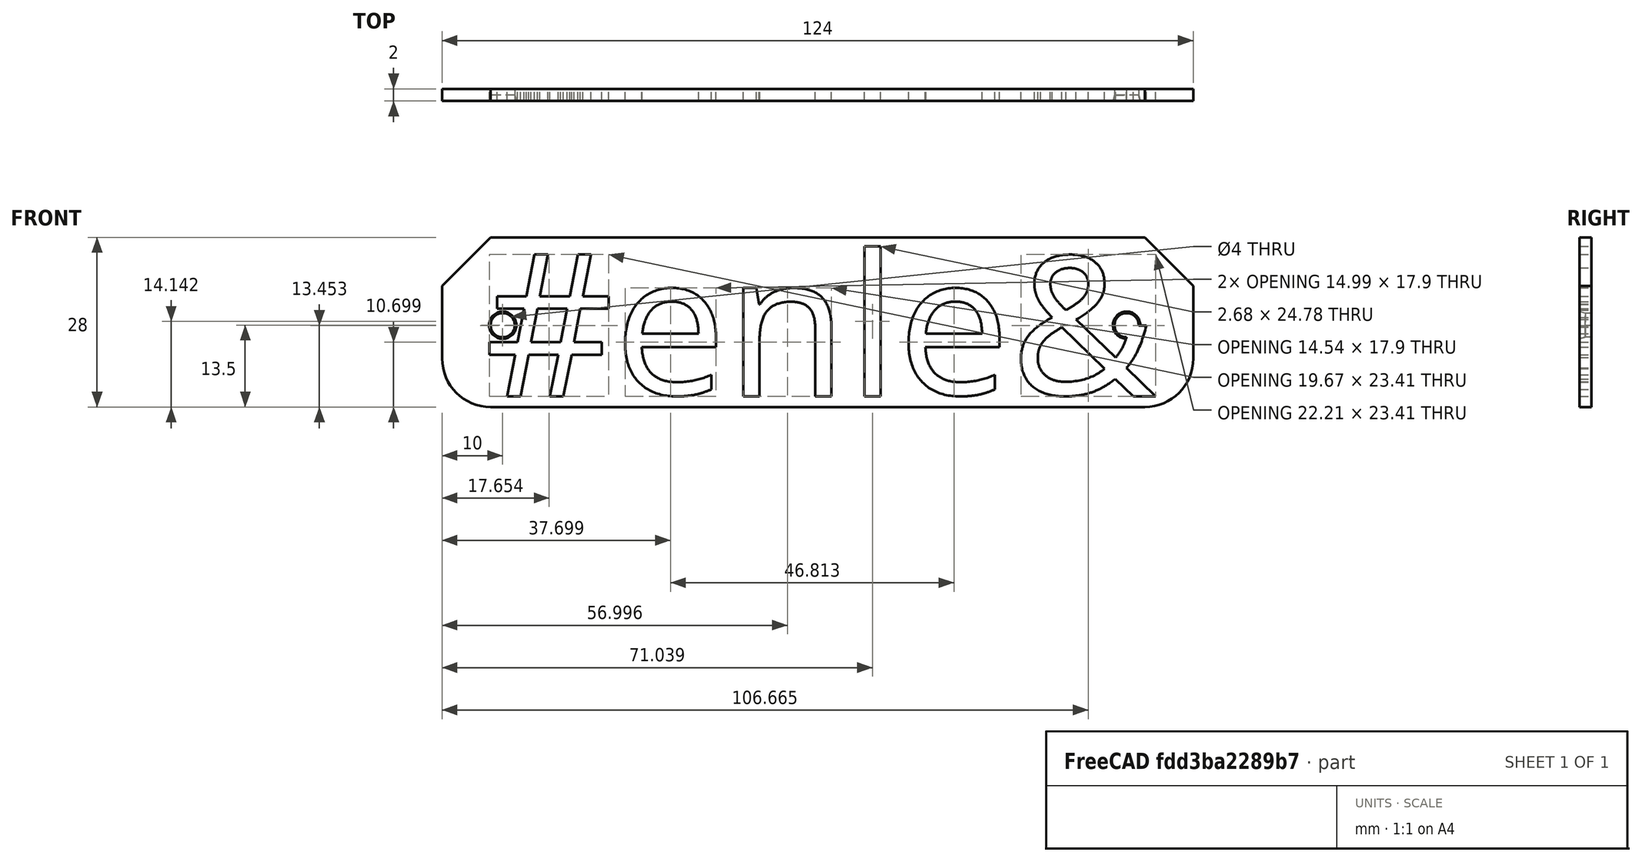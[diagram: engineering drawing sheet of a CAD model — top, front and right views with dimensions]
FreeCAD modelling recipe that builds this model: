
FCSTD DOCUMENT  (FreeCAD 0.19R24276 (Git))
Label: yamahaSR250FuelTankLogo
License: All rights reserved
LicenseURL: http://en.wikipedia.org/wiki/All_rights_reserved
objects: TechDraw::DrawViewDimension×6, Part::Cut×3, TechDraw::DrawProjGroupItem×3, Part::Cylinder×2, Part::Cone×2, Part::MultiFuse×2, TechDraw::DrawSVGTemplate×2, TechDraw::DrawViewPart×2, TechDraw::DrawPage×2, Part::Box×1, Part::Part2DObjectPython×1, Part::Extrusion×1, Part::Chamfer×1, Part::Fillet×1, TechDraw::DrawProjGroup×1, TechDraw::DrawViewAnnotation×1
note: 14 computed .brp shape members not serialized (recipe doc carries the construction recipe); baked Part::Feature solids carry a one-line shape summary decoded from their .brp

FEATURE [Part::Box] Box  label="Cube"
  AttacherType = Attacher::AttachEngine3D
  Height = 28
  Length = 124
  Placement = pos=(0,0,-6.75) rot=(0,0,1;0rad)
  Width = 2
FEATURE [Part::Part2DObjectPython] ShapeString  # Draft 2D object (typed FeaturePython)
  FontFile = <userpath>/Descargas/OpenSans-Regular.ttf
  Placement = pos=(7,0,-5) rot=(1,0,0;1.5708rad)
  Size = 30
  String = #enle&
  Tracking = 0
FEATURE [Part::Extrusion] Extrude
  Base = -> ShapeString
  Dir = (0,2,0)
  DirMode = 0
  FaceMakerClass = Part::FaceMakerExtrusion
  LengthFwd = 0
  LengthRev = 0
  Solid = false
  Symmetric = false
FEATURE [Part::Chamfer] Chamfer
  Base = -> Box
  Edges = 2 edges r=8: [Edge2,Edge6]
FEATURE [Part::Fillet] Fillet
  Base = -> Chamfer
  Edges = 2 edges r=8: [Edge3,Edge13]
FEATURE [Part::Cut] Cut
  Base = -> Fillet
  Tool = -> Extrude
FEATURE [Part::Cylinder] Cylinder
  Angle = 360
  AttacherType = Attacher::AttachEngine3D
  Height = 10
  Placement = pos=(10,2,6.75) rot=(1,0,0;1.5708rad)
  Radius = 2
FEATURE [Part::Cylinder] Cylinder001
  Angle = 360
  AttacherType = Attacher::AttachEngine3D
  Height = 10
  Placement = pos=(113,2,6.75) rot=(1,0,0;1.5708rad)
  Radius = 2
FEATURE [Part::Cone] Cone
  Angle = 360
  AttacherType = Attacher::AttachEngine3D
  Height = 1
  Placement = pos=(10,1,6.75) rot=(1,0,0;1.5708rad)
  Radius1 = 2
  Radius2 = 2.25
FEATURE [Part::Cone] Cone001
  Angle = 360
  AttacherType = Attacher::AttachEngine3D
  Height = 1
  Placement = pos=(113,1,6.75) rot=(1,0,0;1.5708rad)
  Radius1 = 2
  Radius2 = 2.25
FEATURE [Part::MultiFuse] Fusion
  Shapes = -> [Cylinder,Cone]
FEATURE [Part::MultiFuse] Fusion001
  Shapes = -> [Cylinder001,Cone001]
FEATURE [Part::Cut] Cut001
  Base = -> Cut
  Tool = -> Fusion
FEATURE [Part::Cut] Cut002
  Base = -> Cut001
  Tool = -> Fusion001
FEATURE [TechDraw::DrawSVGTemplate] Template
  EditableTexts = Designed_by_Name=<owner>; Drawing_number=001; FC-Date=-; FC-SC=1:1; FC-SH=1/2; FC-Title=SR250FuelTankLogo; Subtitle=Logo Deposito SR250; Weight=<100gr
  Height = 210
  Orientation = 1
  Width = 297
FEATURE [TechDraw::DrawSVGTemplate] Template001
  EditableTexts = Designed_by_Name=<owner>; Drawing_number=001; FC-Date=-; FC-SC=1:1; FC-SH=2/2; FC-Title=SR250FuelTankLogo; Subtitle=Logo Deposito SR250; Weight=<100gr
  Height = 210
  Orientation = 1
  Width = 297
FEATURE [TechDraw::DrawViewPart] View
  CoarseView = false
  Direction = (0.577,-0.577,0.577)
  Focus = 100
  HardHidden = false
  IsoCount = 0
  IsoHidden = false
  IsoVisible = false
  LockPosition = false
  Perspective = false
  Rotation = 0
  ScaleType = 0
  SeamHidden = false
  SeamVisible = true
  SmoothHidden = false
  SmoothVisible = true
  Source = -> [Cut002]
  X = 222.526
  XDirection = (0.707,0.707,0)
  Y = 131.494
FEATURE [TechDraw::DrawProjGroupItem] ProjItem  label="Front"
  CoarseView = false
  Direction = (0,-1,0)
  Focus = 100
  HardHidden = false
  IsoCount = 0
  IsoHidden = false
  IsoVisible = false
  LockPosition = true
  Perspective = false
  Rotation = 0
  RotationVector = (1,0,0)
  ScaleType = 2
  SeamHidden = false
  SeamVisible = true
  SmoothHidden = false
  SmoothVisible = true
  Source = -> [Cut002]
  Type = 0
  X = 0
  XDirection = (1,0,0)
  Y = 0
FEATURE [TechDraw::DrawProjGroupItem] ProjItem001  label="Right"
  CoarseView = false
  Direction = (1,-1e-16,0)
  Focus = 100
  HardHidden = false
  IsoCount = 0
  IsoHidden = false
  IsoVisible = false
  LockPosition = false
  Perspective = false
  Rotation = 0
  RotationVector = (1,0,0)
  ScaleType = 2
  SeamHidden = false
  SeamVisible = true
  SmoothHidden = false
  SmoothVisible = true
  Source = -> [Cut002]
  Type = 2
  X = -78
  XDirection = (1e-16,1,0)
  Y = 0
FEATURE [TechDraw::DrawProjGroupItem] ProjItem002  label="Top"
  CoarseView = false
  Direction = (0,0,1)
  Focus = 100
  HardHidden = false
  IsoCount = 0
  IsoHidden = false
  IsoVisible = false
  LockPosition = false
  Perspective = false
  Rotation = 0
  RotationVector = (1,0,0)
  ScaleType = 2
  SeamHidden = false
  SeamVisible = true
  SmoothHidden = false
  SmoothVisible = true
  Source = -> [Cut002]
  Type = 4
  X = 0
  XDirection = (1,0,0)
  Y = -56
FEATURE [TechDraw::DrawProjGroup] ProjGroup
  Anchor = -> ProjItem
  AutoDistribute = true
  LockPosition = false
  ProjectionType = 0
  Rotation = 0
  ScaleType = 2
  Source = -> [Cut002]
  Views = -> [ProjItem,ProjItem001,ProjItem002]
  X = 100.188
  Y = 152.922
  spacingX = 15
  spacingY = 15
FEATURE [TechDraw::DrawViewDimension] Dimension
  Arbitrary = false
  ArbitraryTolerances = false
  EqualTolerance = true
  FormatSpec = %.2f
  FormatSpecOverTolerance = %+.2f
  FormatSpecUnderTolerance = %+.2f
  Inverted = false
  LockPosition = false
  MeasureType = 1
  OverTolerance = 0
  References2D = -> [ProjItem]
  Rotation = 0
  ScaleType = 0
  TheoreticalExact = false
  Type = 1
  UnderTolerance = 0
  X = -3.21086
  Y = -27.241
FEATURE [TechDraw::DrawViewDimension] Dimension001
  Arbitrary = false
  ArbitraryTolerances = false
  EqualTolerance = true
  FormatSpec = %.2f
  FormatSpecOverTolerance = %+.2f
  FormatSpecUnderTolerance = %+.2f
  Inverted = false
  LockPosition = false
  MeasureType = 1
  OverTolerance = 0
  References2D = -> [ProjItem]
  Rotation = 0
  ScaleType = 0
  TheoreticalExact = false
  Type = 2
  UnderTolerance = 0
  X = 62.1506
  Y = -0.493978
FEATURE [TechDraw::DrawViewDimension] Dimension002
  Arbitrary = false
  ArbitraryTolerances = false
  EqualTolerance = true
  FormatSpec = %.2f
  FormatSpecOverTolerance = %+.2f
  FormatSpecUnderTolerance = %+.2f
  Inverted = false
  LockPosition = false
  MeasureType = 1
  OverTolerance = 0
  References2D = -> [ProjItem001]
  Rotation = 0
  ScaleType = 0
  TheoreticalExact = false
  Type = 1
  UnderTolerance = 0
  X = 0
  Y = -28.0784
FEATURE [TechDraw::DrawPage] Page  label="Vistas"
  KeepUpdated = true
  NextBalloonIndex = 1
  ProjectionType = 0
  Template = -> Template
  Views = -> [View,ProjGroup,Dimension,Dimension001,Dimension002]
FEATURE [TechDraw::DrawViewPart] View001
  CoarseView = false
  Direction = (0.577,-0.577,0.577)
  Focus = 100
  HardHidden = false
  IsoCount = 0
  IsoHidden = false
  IsoVisible = false
  LockPosition = false
  Perspective = false
  Rotation = 0
  ScaleType = 0
  SeamHidden = false
  SeamVisible = true
  SmoothHidden = false
  SmoothVisible = true
  Source = -> [Cut002]
  X = 149.7
  XDirection = (0.707,0.707,0)
  Y = 121.8
FEATURE [TechDraw::DrawViewDimension] Dimension003
  Arbitrary = false
  ArbitraryTolerances = false
  EqualTolerance = true
  FormatSpec = %.2f
  FormatSpecOverTolerance = %+.2f
  FormatSpecUnderTolerance = %+.2f
  Inverted = false
  LockPosition = false
  MeasureType = 1
  OverTolerance = 0
  References2D = -> [View001]
  Rotation = 0
  ScaleType = 0
  TheoreticalExact = false
  Type = 0
  UnderTolerance = 0
  X = -74.1267
  Y = 30.8947
FEATURE [TechDraw::DrawViewDimension] Dimension004
  Arbitrary = false
  ArbitraryTolerances = false
  EqualTolerance = true
  FormatSpec = %.2f
  FormatSpecOverTolerance = %+.2f
  FormatSpecUnderTolerance = %+.2f
  Inverted = false
  LockPosition = false
  MeasureType = 1
  OverTolerance = 0
  References2D = -> [View001]
  Rotation = 0
  ScaleType = 0
  TheoreticalExact = false
  Type = 2
  UnderTolerance = 0
  X = 61.4206
  Y = 1.05474
FEATURE [TechDraw::DrawViewDimension] Dimension005
  Arbitrary = false
  ArbitraryTolerances = false
  EqualTolerance = true
  FormatSpec = %.2f
  FormatSpecOverTolerance = %+.2f
  FormatSpecUnderTolerance = %+.2f
  Inverted = false
  LockPosition = false
  MeasureType = 1
  OverTolerance = 0
  References2D = -> [View001]
  Rotation = 0
  ScaleType = 0
  TheoreticalExact = false
  Type = 0
  UnderTolerance = 0
  X = -59.7749
  Y = -9.50932
FEATURE [TechDraw::DrawViewAnnotation] Annotation
  Font = osifont
  LineSpace = 80
  LockPosition = false
  MaxWidth = -1
  Rotation = 0
  ScaleType = 0
  Text = Aproximate measurements: | Check with 3D piece
  TextSize = 5
  TextStyle = 0
  X = 67.7
  Y = 73
FEATURE [TechDraw::DrawPage] Page001  label="Cotas"
  KeepUpdated = true
  NextBalloonIndex = 1
  ProjectionType = 0
  Template = -> Template001
  Views = -> [View001,Dimension003,Dimension004,Dimension005,Annotation]
